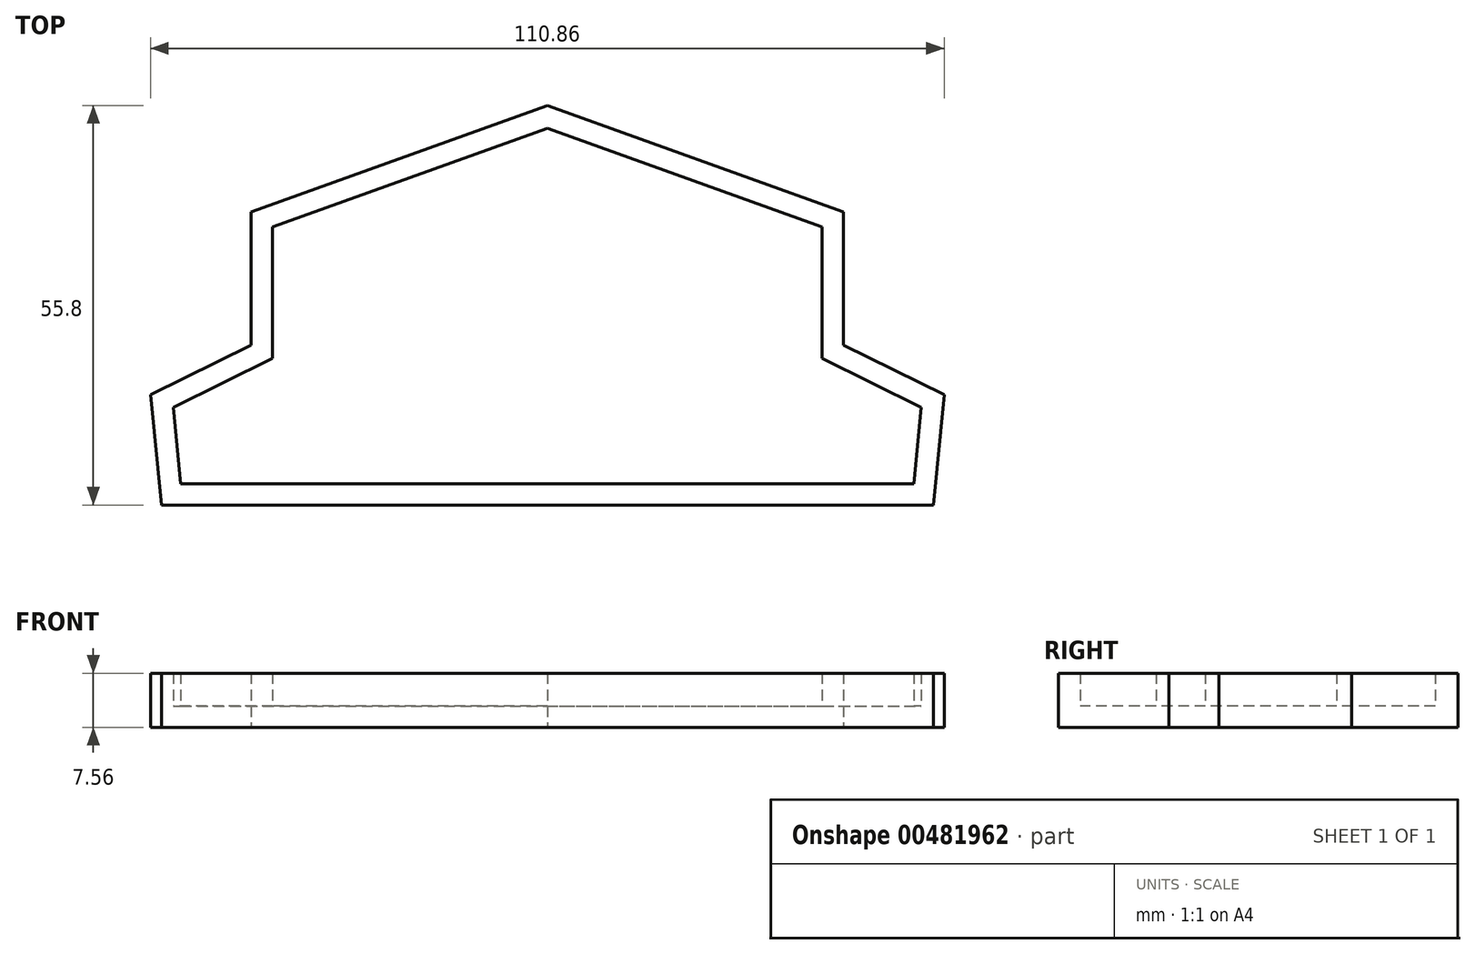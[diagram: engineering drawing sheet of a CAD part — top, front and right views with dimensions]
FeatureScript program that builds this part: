
annotation { "Feature Type Name" : "Feature", "Feature Type Description" : "" }
export const myFeature = defineFeature(function(context is Context, id is Id, definition is map)
    precondition{}
    {
        {
            var Q0;
            Q0=qCreatedBy(makeId("Top.planeOp"),FACE);
            var sketch = newSketch(context, id + "F0", { "sketchPlane" : qUnion([Q0])});
            skLineSegment(sketch, "E0", {"start": v(0, 33.44) * mm, "end": v(-41.38, 18.59) * mm});
            skLineSegment(sketch, "E1", {"start": v(-41.38, 18.59) * mm, "end": v(-41.38, 0) * mm});
            skLineSegment(sketch, "E2", {"start": v(-41.38, 0) * mm, "end": v(-55.43, -6.98) * mm});
            skLineSegment(sketch, "E3", {"start": v(-55.43, -6.98) * mm, "end": v(-53.92, -22.36) * mm});
            skLineSegment(sketch, "E4", {"start": v(-53.92, -22.36) * mm, "end": v(0, -22.36) * mm});
            skLineSegment(sketch, "E5", {"start": v(0, -22.36) * mm, "end": v(0, 33.44) * mm, "construction": true});
            skLineSegment(sketch, "E6.MirrorCS", {"start": v(0, 33.44) * mm, "end": v(41.38, 18.59) * mm});
            skLineSegment(sketch, "E7.MirrorCS", {"start": v(41.38, 18.59) * mm, "end": v(41.38, 0) * mm});
            skLineSegment(sketch, "E8.MirrorCS", {"start": v(55.43, -6.98) * mm, "end": v(53.92, -22.36) * mm});
            skLineSegment(sketch, "E9.MirrorCS", {"start": v(41.38, 0) * mm, "end": v(55.43, -6.98) * mm});
            skLineSegment(sketch, "E10.MirrorCS", {"start": v(53.92, -22.36) * mm, "end": v(0, -22.36) * mm});
            skSolve(sketch);
        }
        {
            var Q0;
            Q0 = qSketchRegion(id + "F0", true);
            extrude(context, id + "F1", {"entities" : qUnion([Q0]), "depth" : 7.56 * mm});
        }
        {
            var Q0;
            Q0=makeQuery(id+"F1.opExtrude","CAP_FACE",FACE,{"disambiguationData":[OSD([sQuery(id+"F0.wireOp",EDGE,"E0"),sQuery(id+"F0.wireOp",EDGE,"E1"),sQuery(id+"F0.wireOp",EDGE,"E2"),sQuery(id+"F0.wireOp",EDGE,"E3"),sQuery(id+"F0.wireOp",EDGE,"E4"),sQuery(id+"F0.wireOp",EDGE,"E6.MirrorCS"),sQuery(id+"F0.wireOp",EDGE,"E7.MirrorCS"),sQuery(id+"F0.wireOp",EDGE,"E8.MirrorCS"),sQuery(id+"F0.wireOp",EDGE,"E9.MirrorCS"),sQuery(id+"F0.wireOp",EDGE,"E10.MirrorCS")])],"isStart":false});
            shell(context, id + "F2", {"entities" : qUnion([Q0]), "thickness" : 3 * mm});
        }
    });
